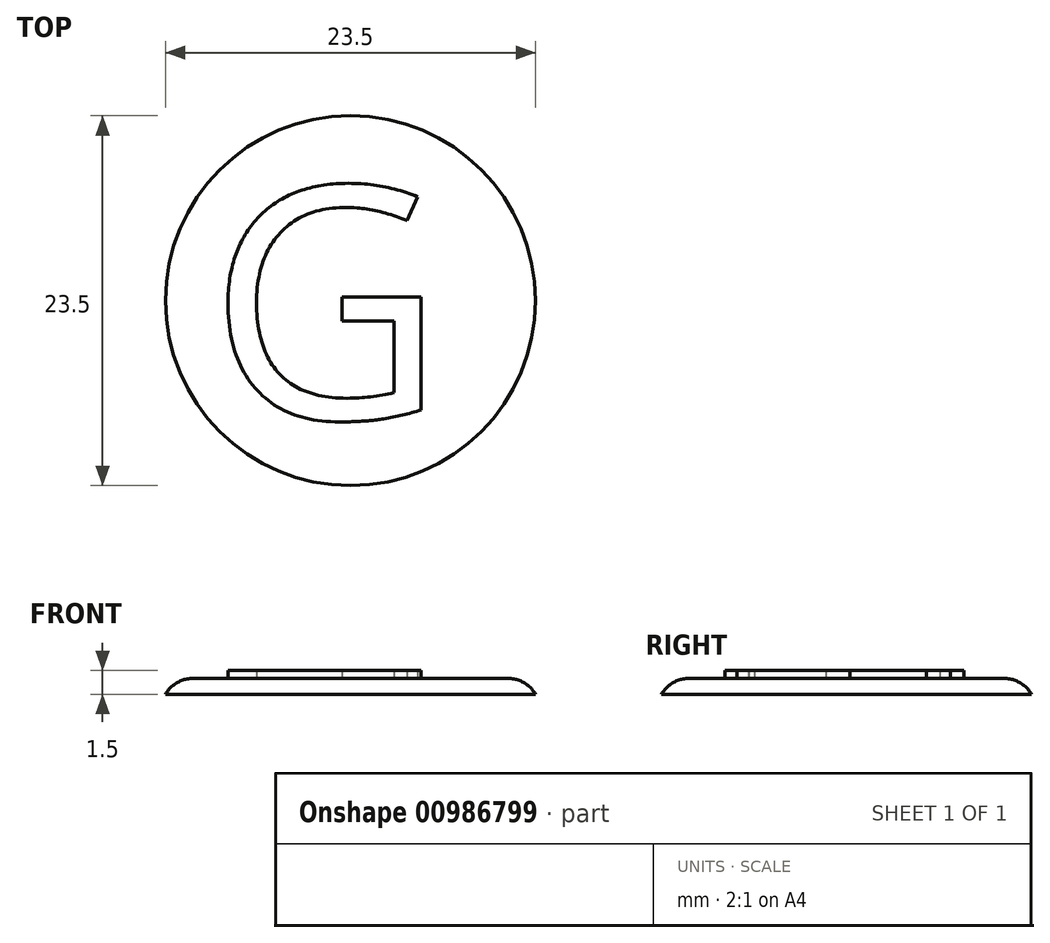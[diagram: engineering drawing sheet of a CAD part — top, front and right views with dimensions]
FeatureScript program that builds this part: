
annotation { "Feature Type Name" : "Feature", "Feature Type Description" : "" }
export const myFeature = defineFeature(function(context is Context, id is Id, definition is map)
    precondition{}
    {
        {
            var Q0;
            Q0=qCreatedBy(makeId("Top.planeOp"),FACE);
            var sketch = newSketch(context, id + "F0", { "sketchPlane" : qUnion([Q0])});
            skCircle(sketch, "E0", {"center": v(0, 0) * mm, "radius": 11.75 * mm});
            skSolve(sketch);
        }
        {
            var Q0;
            Q0=makeQuery(id+"F0.imprint","IMPRINT",FACE,{"disambiguationData":[TD([[makeQuery(id+"F0.imprint","IMPRINT",EDGE,{"derivedFrom":sQuery(id+"F0.wireOp",EDGE,"E0")}),1.0]])]});
            extrude(context, id + "F1", {"entities" : qUnion([Q0]), "depth" : 1 * mm, "offsetDistance" : 25 * mm});
        }
        {
            var Q0;
            Q0=makeQuery(id+"F1.opExtrude","CAP_FACE",FACE,{"disambiguationData":[OSD([sQuery(id+"F0.wireOp",EDGE,"E0")])],"isStart":false});
            var sketch = newSketch(context, id + "F2", { "sketchPlane" : qUnion([Q0])});
            skText(sketch, "E1", { "text": "G", "fontName": "OpenSans-Regular.ttf"});
            const initialGuessF2  = {"E1": [-0.00904, -0.0075, 1, 0, 0.01487]};
            skSetInitialGuess(sketch, initialGuessF2);
            skSolve(sketch);
        }
        {
            var Q0;
            Q0 = qSketchRegion(id + "F2", true);
            extrude(context, id + "F3", {"entities" : qUnion([Q0]), "operationType" : NewBodyOperationType.ADD, "depth" : 0.5 * mm, "offsetDistance" : 25 * mm});
        }
        {
            var Q0;
            Q0=makeQuery(id+"F1.opExtrude","CAP_EDGE",EDGE,{"disambiguationData":[OSD([sQuery(id+"F0.wireOp",EDGE,"E0")])],"isStart":false});
            fillet(context, id + "F4", {"entities" : qUnion([Q0]), "radius" : 2 * mm, "allowEdgeOverflow" : false});
        }
    });
